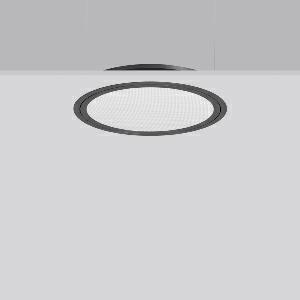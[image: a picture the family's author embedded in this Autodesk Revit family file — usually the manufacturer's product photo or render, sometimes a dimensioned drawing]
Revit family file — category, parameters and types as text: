
# Revit family: triona_round_e_312423_0031_1_12_85fb
name_source: partatom
category: Lighting Fixtures
units: mm (PartAtom-declared; Revit-internal decimal feet)

## family parameters
Cut with Voids When Loaded = No
Host = Face
Light Source = No
Part Type = Normal
Room Calculation Point = No
Round Connector Dimension = Use Diameter
Shared = No

## types (1)
- TRIONA round E (1 x LED Modul 840, 3250 lm, 4000)
    Apparent Load = 28 VA
    CIE Flux Codes = 58 87 97 100 100
    Color Rendering = 80
    Color Temperature = 4000
    Default Elevation = 1800 mm
    Description = Series: TRIONA round
Decorative round LED recessed surface luminaire. Cover made of sheet steel, powder-coated. Frame made of aluminium, powder-coated. Recessed ring: aluminium extrusion profile, powder coated. Light emission through a diffuser in plastic, opal/prismatic. Lightguide and diffuser made of non-yellowing plastic (PMMA). Lateral light emission (RZB SIDELITE technology) for above-average homogeneous light distribution. Suitable for installation in cavity ceilings. Tool-free mounting system thanks to the rocker arm mechanism (patent pending). Electronic ballast included. Very easy installation thanks to Plug+Play connection. 
Colour: anthracite metallic (DB703)
Diameter: 505 mm
Height: 2 mm
Cut-out diameter: 482 mm
Recess height: 100 mm
Luminaire: recess height: 89 mm
Lamp: LED
Socket: without socket
Colour temperature: 4000K
Colour rendering index (CRI): 80
System power: 28 W
Rated luminous flux: 3250 lm
Luminous efficiency: 116 lm/W
Control gear: Converter, dimmable, DALI
Protection class: I
Type of protection: IP 40
    Height = 0 mm  [stored 0 ft]
    Lamp = 1 x LED Modul 840
    Lamp Light Flux = 3250 lm
    Lamp count = 1
    Length = 505 mm
    Lifetime = 50000 h
    Luminous efficacy = 116 lm/W
    Manufacturer = RZB
    ModVariant = No
    Model = 312423.0031.1.12
    Mounting Place = Ceiling
    Mounting Type = Recessed
    Number of Poles = 1
    OnlyDefault = Yes
    Power Factor = 1
    Product Name = TRIONA round E
    Product group = Recessed modular luminaires
    ProductGroupID = 406
    Protection Class = Protection class I
    Protection Degree = IP 20
    RLX_Detail_Level = 1
    RLX_Emergency_Light_Flux = 0 lm
    RLX_Emergency_Type = 0
    RLX_Emergency_Type_DB = No
    RlxData = <blob elided: 34877 chars, md5=593eff42>
    Socket = socket
    Standby Power = 0 W
    System Light Flux = 3250 lm
    System Power = 28 W
    Type Comments = Product without accessories
    Type Image = 312423.0031.12.jpg
    URL = http://relux.com
    VarID = ---
    Voltage = 230 V
    Voltage Range = 220-240 V
    Weight = 0.00 kg
    Width = 0 mm  [stored 0 ft]

note: [stored X ft] marks values corroborated as IEEE doubles in the binary element streams (Revit-internal decimal feet)

## geometry (parser evidence)
native form markers: Blend x4, Sweep x7
no freeform markers — native parametric forms only
